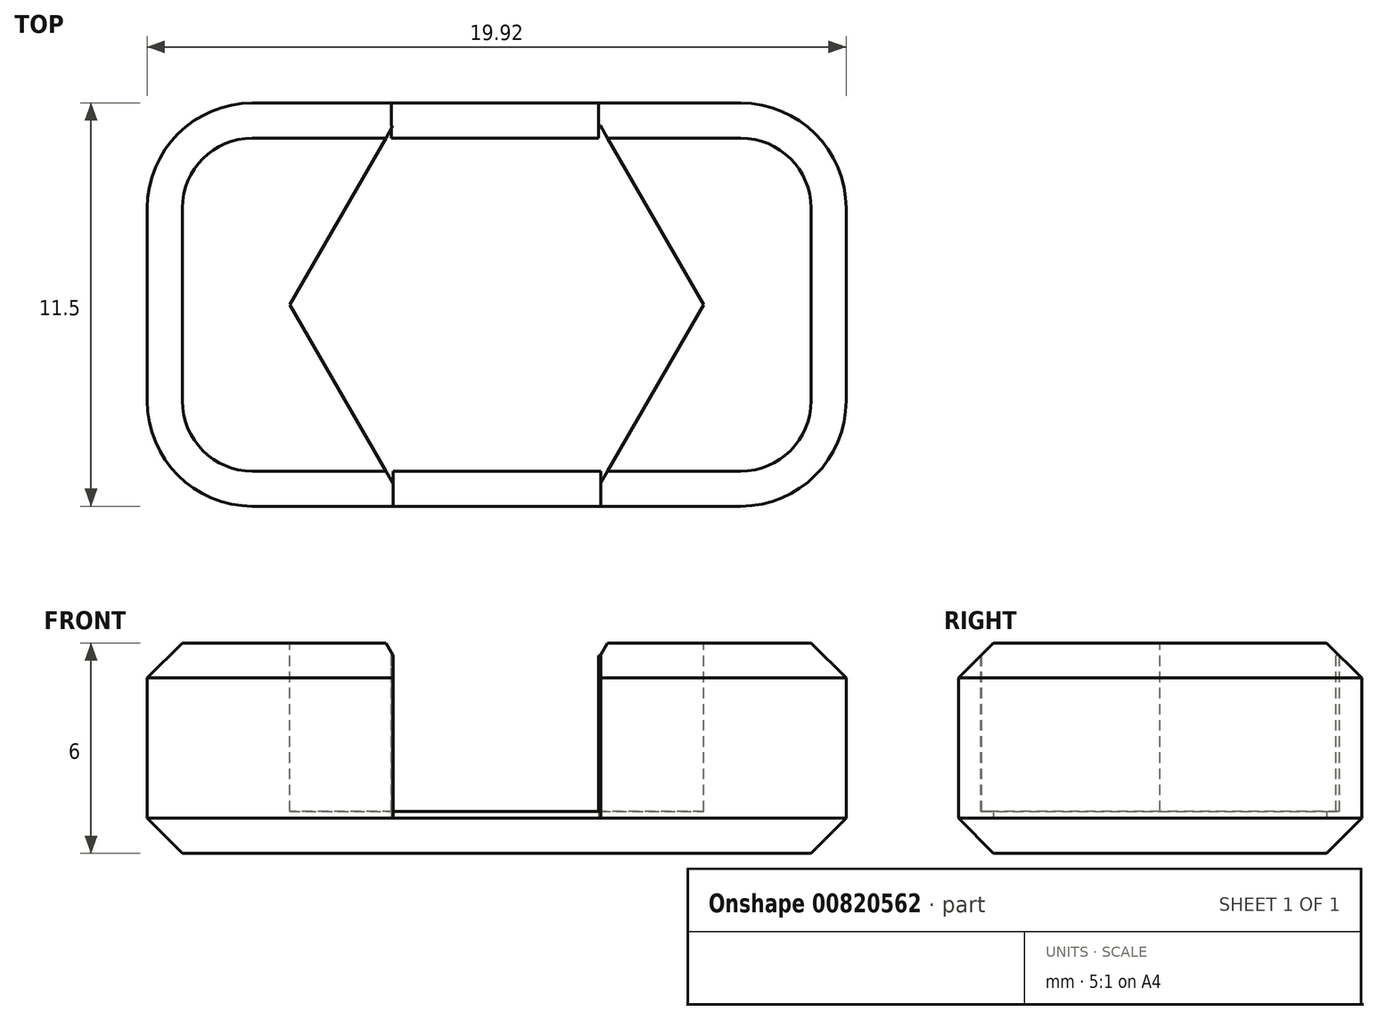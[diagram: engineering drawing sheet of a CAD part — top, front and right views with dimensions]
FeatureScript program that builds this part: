
annotation { "Feature Type Name" : "Feature", "Feature Type Description" : "" }
export const myFeature = defineFeature(function(context is Context, id is Id, definition is map)
    precondition{}
    {
        {
            var Q0;
            Q0=qCreatedBy(makeId("Top.planeOp"),FACE);
            var sketch = newSketch(context, id + "F0", { "sketchPlane" : qUnion([Q0])});
            skLineSegment(sketch, "E0.bottom", {"start": v(-6.96, 5.75) * mm, "end": v(6.96, 5.75) * mm});
            skLineSegment(sketch, "E0.top", {"start": v(-6.96, -5.75) * mm, "end": v(6.96, -5.75) * mm});
            skLineSegment(sketch, "E0.left", {"start": v(-9.96, 2.75) * mm, "end": v(-9.96, -2.75) * mm});
            skLineSegment(sketch, "E0.right", {"start": v(9.96, 2.75) * mm, "end": v(9.96, -2.75) * mm});
            skPoint(sketch, "E0.middle", {"position": v(0, 0) * mm});
            skPoint(sketch, "E1.visualSharp", {"position": v(-9.96, 5.75) * mm});
            skArc(sketch, "E1.filletArc", {"start": v(-6.96, 5.75) * mm, "mid": v(-9.08, 4.87) * mm, "end": v(-9.96, 2.75) * mm});
            skPoint(sketch, "E2.visualSharp", {"position": v(9.96, 5.75) * mm});
            skArc(sketch, "E2.filletArc", {"start": v(9.96, 2.75) * mm, "mid": v(9.08, 4.87) * mm, "end": v(6.96, 5.75) * mm});
            skPoint(sketch, "E3.visualSharp", {"position": v(9.96, -5.75) * mm});
            skArc(sketch, "E3.filletArc", {"start": v(6.96, -5.75) * mm, "mid": v(9.08, -4.87) * mm, "end": v(9.96, -2.75) * mm});
            skPoint(sketch, "E4.visualSharp", {"position": v(-9.96, -5.75) * mm});
            skArc(sketch, "E4.filletArc", {"start": v(-9.96, -2.75) * mm, "mid": v(-9.08, -4.87) * mm, "end": v(-6.96, -5.75) * mm});
            skSolve(sketch);
        }
        {
            var Q0;
            Q0=makeQuery(id+"F0.imprint","IMPRINT",FACE,{"disambiguationData":[TD([[makeQuery(id+"F0.imprint","IMPRINT",EDGE,{"derivedFrom":sQuery(id+"F0.wireOp",EDGE,"E0.bottom")}),-1.0]])]});
            extrude(context, id + "F1", {"entities" : qUnion([Q0]), "depth" : 6 * mm, "offsetDistance" : 25 * mm});
        }
        {
            var Q0;
            Q0=makeQuery(id+"F1.opExtrude","CAP_FACE",FACE,{"disambiguationData":[OSD([sQuery(id+"F0.wireOp",EDGE,"E0.bottom"),sQuery(id+"F0.wireOp",EDGE,"E0.top"),sQuery(id+"F0.wireOp",EDGE,"E0.left"),sQuery(id+"F0.wireOp",EDGE,"E0.right"),sQuery(id+"F0.wireOp",EDGE,"E1.filletArc"),sQuery(id+"F0.wireOp",EDGE,"E2.filletArc"),sQuery(id+"F0.wireOp",EDGE,"E3.filletArc"),sQuery(id+"F0.wireOp",EDGE,"E4.filletArc")])],"isStart":false});
            var sketch = newSketch(context, id + "F2", { "sketchPlane" : qUnion([Q0])});
            skCircle(sketch, "E5.cCircle", {"center": v(0, 0) * mm, "radius": 5.9 * mm, "construction": true});
            skLineSegment(sketch, "E5.0", {"start": v(-2.95, 5.1) * mm, "end": v(2.95, 5.1) * mm});
            skLineSegment(sketch, "E5.1", {"start": v(2.95, 5.1) * mm, "end": v(5.9, 0) * mm});
            skLineSegment(sketch, "E5.2", {"start": v(5.9, 0) * mm, "end": v(2.95, -5.1) * mm});
            skLineSegment(sketch, "E5.3", {"start": v(2.95, -5.1) * mm, "end": v(-2.95, -5.1) * mm});
            skLineSegment(sketch, "E5.4", {"start": v(-2.95, -5.1) * mm, "end": v(-5.9, 0) * mm});
            skLineSegment(sketch, "E5.5", {"start": v(-5.9, 0) * mm, "end": v(-2.95, 5.1) * mm});
            skSolve(sketch);
        }
        {
            var Q0;
            Q0 = qSketchRegion(id + "F2", true);
            extrude(context, id + "F3", {"entities" : qUnion([Q0]), "operationType" : NewBodyOperationType.REMOVE, "oppositeDirection" : true, "depth" : 4.8 * mm, "offsetDistance" : 25 * mm});
        }
        {
            var Q0;
            Q0=makeQuery(id+"F1.opExtrude","CAP_EDGE",EDGE,{"disambiguationData":[OSD([sQuery(id+"F0.wireOp",EDGE,"E0.bottom")])],"isStart":false});
            var Q1;
            Q1=makeQuery(id+"F1.opExtrude","CAP_EDGE",EDGE,{"disambiguationData":[OSD([sQuery(id+"F0.wireOp",EDGE,"E0.bottom")])],"isStart":true});
            chamfer(context, id + "F4", {"entities" : qUnion([Q0, Q1]), "width" : 1 * mm, "tangentPropagation" : true});
        }
        {
            var Q0;
            Q0=makeQuery(id+"F1.opExtrude","SWEPT_FACE",FACE,{"disambiguationData":[OSD([sQuery(id+"F0.wireOp",EDGE,"E0.top")])]});
            var sketch = newSketch(context, id + "F5", { "sketchPlane" : qUnion([Q0])});
            skLineSegment(sketch, "E6", {"start": v(-2.95, 5.66) * mm, "end": v(-2.95, 1) * mm, "construction": true});
            skLineSegment(sketch, "E7", {"start": v(2.96, 5.65) * mm, "end": v(2.96, 1) * mm, "construction": true});
            skLineSegment(sketch, "E8.bottom", {"start": v(-2.95, 5.66) * mm, "end": v(2.96, 5.66) * mm});
            skLineSegment(sketch, "E8.top", {"start": v(-2.95, 1) * mm, "end": v(2.96, 1) * mm});
            skLineSegment(sketch, "E8.left", {"start": v(-2.95, 5.66) * mm, "end": v(-2.95, 1) * mm});
            skLineSegment(sketch, "E8.right", {"start": v(2.96, 5.66) * mm, "end": v(2.96, 1) * mm});
            skSolve(sketch);
        }
        {
            var Q0;
            Q0 = qSketchRegion(id + "F5", true);
            extrude(context, id + "F6", {"entities" : qUnion([Q0]), "operationType" : NewBodyOperationType.REMOVE, "oppositeDirection" : true, "depth" : 1 * mm, "offsetDistance" : 25 * mm});
        }
        {
            var Q0;
            Q0=makeQuery(id+"F1.opExtrude","SWEPT_FACE",FACE,{"disambiguationData":[OSD([sQuery(id+"F0.wireOp",EDGE,"E0.bottom")])]});
            var sketch = newSketch(context, id + "F7", { "sketchPlane" : qUnion([Q0])});
            skLineSegment(sketch, "E9", {"start": v(-2.9, 5.65) * mm, "end": v(-2.9, 1) * mm, "construction": true});
            skLineSegment(sketch, "E10", {"start": v(3, 5.7) * mm, "end": v(3, 1) * mm, "construction": true});
            skLineSegment(sketch, "E11.bottom", {"start": v(-2.9, 5.65) * mm, "end": v(3, 5.65) * mm});
            skLineSegment(sketch, "E11.top", {"start": v(-2.9, 1) * mm, "end": v(3, 1) * mm});
            skLineSegment(sketch, "E11.left", {"start": v(-2.9, 5.65) * mm, "end": v(-2.9, 1) * mm});
            skLineSegment(sketch, "E11.right", {"start": v(3, 5.65) * mm, "end": v(3, 1) * mm});
            skSolve(sketch);
        }
        {
            var Q0;
            Q0 = qSketchRegion(id + "F7", true);
            extrude(context, id + "F8", {"entities" : qUnion([Q0]), "operationType" : NewBodyOperationType.REMOVE, "oppositeDirection" : true, "depth" : 1 * mm, "offsetDistance" : 25 * mm});
        }
    });
